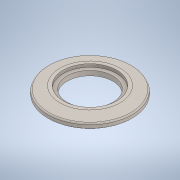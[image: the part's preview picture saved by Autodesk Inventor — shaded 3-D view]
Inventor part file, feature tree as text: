
AUTODESK INVENTOR PART (.ipt)
format: ipt  version: 2021 (Build 250183000, 183)  size: 161,280 bytes
history: native  units: in
note: dims shown in document units (in); Inventor stores cm internally (conversion verified against a paired STEP export)
features: extrude x2, sketch x2, chamfer x1
ambient origin geometry x8: Origin, YZ Plane, XZ Plane, XY Plane, X Axis, Y Axis, Z Axis, Center Point
bodies: Solid1 (feature_tree)
feature tree (5):
  extrude  "Extrusion1"  TaperAngle=0.0deg  [1 undecoded]
  extrude  "Extrusion2"  Depth=0.0787in TaperAngle=0.0deg
  sketch  "Sketch1"  dims[d0=1.1811in d1=0.0in d2=0.0in]
  sketch  "Sketch2"  dims[d3=1.378in d4=0.0787in d5=0.0in]
  chamfer  "Chamfer1"  [1 undecoded]
note: 2 required parameter values undecoded (feature->parameter linkage not recoverable at this tier; creation-order binding heuristic only, values carry confidence <= 0.55)
